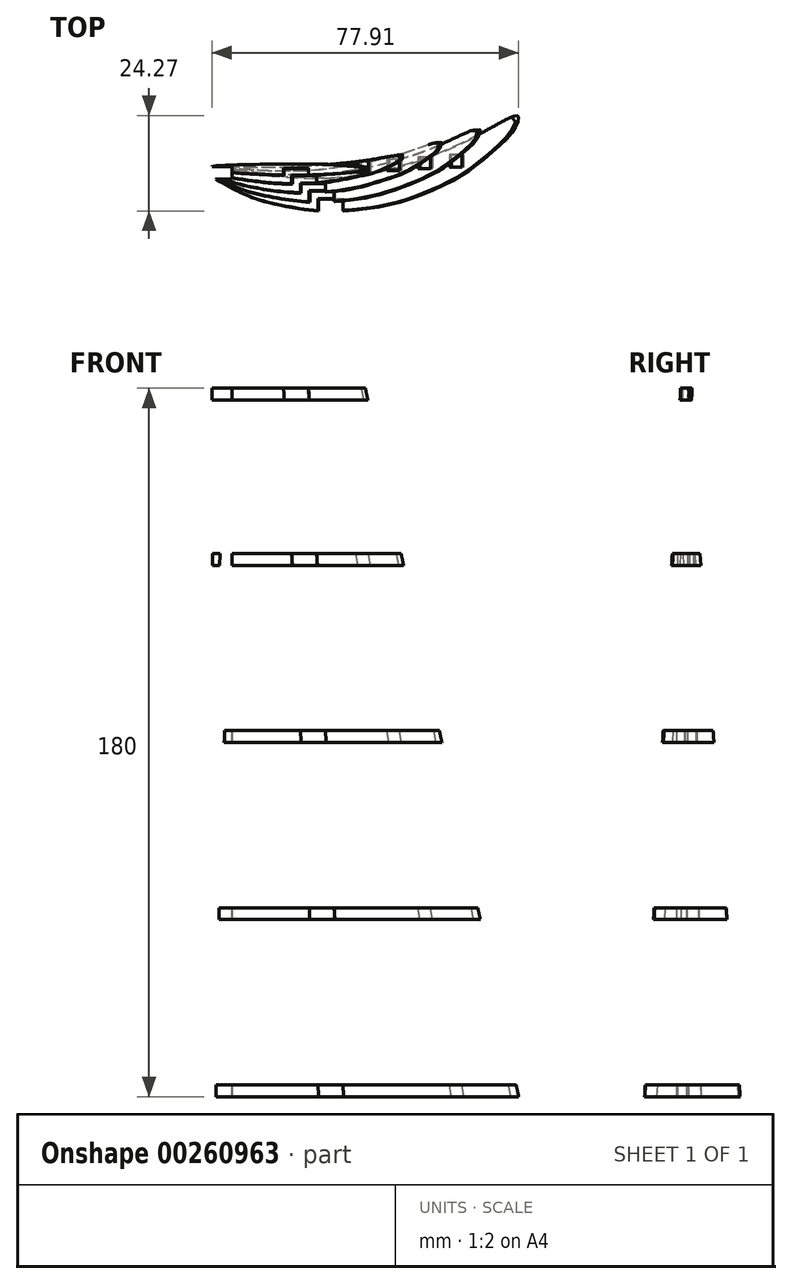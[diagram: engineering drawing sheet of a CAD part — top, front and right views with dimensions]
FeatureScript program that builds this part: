
annotation { "Feature Type Name" : "Feature", "Feature Type Description" : "" }
export const myFeature = defineFeature(function(context is Context, id is Id, definition is map)
    precondition{}
    {
        {
            var Q0;
            Q0=qCreatedBy(makeId("Top.planeOp"),FACE);
            var sketch = newSketch(context, id + "F0", { "sketchPlane" : qUnion([Q0])});
            skLineSegment(sketch, "E0", {"start": v(1.36, -2.16) * mm, "end": v(0.8, -1.48) * mm});
            skLineSegment(sketch, "E1", {"start": v(0.8, -1.48) * mm, "end": v(0.54, -1.16) * mm});
            skLineSegment(sketch, "E2", {"start": v(0.54, -1.16) * mm, "end": v(0.32, -0.85) * mm});
            skLineSegment(sketch, "E3", {"start": v(0.32, -0.85) * mm, "end": v(0.15, -0.57) * mm});
            skLineSegment(sketch, "E4", {"start": v(0.15, -0.57) * mm, "end": v(0.04, -0.32) * mm});
            skLineSegment(sketch, "E5", {"start": v(0.04, -0.32) * mm, "end": v(0, -0.1) * mm});
            skLineSegment(sketch, "E6", {"start": v(0, -0.1) * mm, "end": v(0, 0) * mm});
            skLineSegment(sketch, "E7", {"start": v(0, 0) * mm, "end": v(0.14, 0.2) * mm});
            skLineSegment(sketch, "E8", {"start": v(0.14, 0.2) * mm, "end": v(0.34, 0.3) * mm});
            skLineSegment(sketch, "E9", {"start": v(0.34, 0.3) * mm, "end": v(0.6, 0.35) * mm});
            skLineSegment(sketch, "E10", {"start": v(0.6, 0.35) * mm, "end": v(0.9, 0.37) * mm});
            skLineSegment(sketch, "E11", {"start": v(0.9, 0.37) * mm, "end": v(1.27, 0.37) * mm});
            skLineSegment(sketch, "E12", {"start": v(1.27, 0.37) * mm, "end": v(1.67, 0.35) * mm});
            skLineSegment(sketch, "E13", {"start": v(1.67, 0.35) * mm, "end": v(2.54, 0.25) * mm});
            skLineSegment(sketch, "E14", {"start": v(2.54, 0.25) * mm, "end": v(3.67, 0.08) * mm});
            skLineSegment(sketch, "E15", {"start": v(3.67, 0.08) * mm, "end": v(5.17, -0.16) * mm});
            skLineSegment(sketch, "E16", {"start": v(5.17, -0.16) * mm, "end": v(5.97, -0.3) * mm});
            skLineSegment(sketch, "E17", {"start": v(5.97, -0.3) * mm, "end": v(6.72, -0.43) * mm});
            skLineSegment(sketch, "E18", {"start": v(6.72, -0.43) * mm, "end": v(7.44, -0.55) * mm});
            skLineSegment(sketch, "E19", {"start": v(7.44, -0.55) * mm, "end": v(8.78, -0.8) * mm});
            skLineSegment(sketch, "E20", {"start": v(8.78, -0.8) * mm, "end": v(10.03, -1.02) * mm});
            skLineSegment(sketch, "E21", {"start": v(10.03, -1.02) * mm, "end": v(11.21, -1.23) * mm});
            skLineSegment(sketch, "E22", {"start": v(11.21, -1.23) * mm, "end": v(13.97, -1.68) * mm});
            skLineSegment(sketch, "E23", {"start": v(13.97, -1.68) * mm, "end": v(14.7, -1.78) * mm});
            skLineSegment(sketch, "E24", {"start": v(14.7, -1.78) * mm, "end": v(15.94, -1.94) * mm});
            skLineSegment(sketch, "E25", {"start": v(15.94, -1.94) * mm, "end": v(17.2, -2.08) * mm});
            skLineSegment(sketch, "E26", {"start": v(17.2, -2.08) * mm, "end": v(18.5, -2.2) * mm});
            skLineSegment(sketch, "E27", {"start": v(18.5, -2.2) * mm, "end": v(21.19, -2.42) * mm});
            skLineSegment(sketch, "E28", {"start": v(21.19, -2.42) * mm, "end": v(23.95, -2.56) * mm});
            skLineSegment(sketch, "E29", {"start": v(23.95, -2.56) * mm, "end": v(26.74, -2.62) * mm});
            skLineSegment(sketch, "E30", {"start": v(26.74, -2.62) * mm, "end": v(30.9, -2.55) * mm});
            skLineSegment(sketch, "E31", {"start": v(30.9, -2.55) * mm, "end": v(32.3, -2.49) * mm});
            skLineSegment(sketch, "E32", {"start": v(32.3, -2.49) * mm, "end": v(35, -2.28) * mm});
            skLineSegment(sketch, "E33", {"start": v(35, -2.28) * mm, "end": v(37.68, -1.98) * mm});
            skLineSegment(sketch, "E34", {"start": v(37.68, -1.98) * mm, "end": v(40.32, -1.59) * mm});
            skLineSegment(sketch, "E35", {"start": v(40.32, -1.59) * mm, "end": v(42.94, -1.1) * mm});
            skLineSegment(sketch, "E36", {"start": v(42.94, -1.1) * mm, "end": v(45.56, -0.51) * mm});
            skLineSegment(sketch, "E37", {"start": v(45.56, -0.51) * mm, "end": v(48.18, 0.16) * mm});
            skLineSegment(sketch, "E38", {"start": v(48.18, 0.16) * mm, "end": v(50.38, 0.8) * mm});
            skLineSegment(sketch, "E39", {"start": v(50.38, 0.8) * mm, "end": v(53.48, 1.8) * mm});
            skLineSegment(sketch, "E40", {"start": v(53.48, 1.8) * mm, "end": v(56.12, 2.73) * mm});
            skLineSegment(sketch, "E41", {"start": v(56.12, 2.73) * mm, "end": v(58.71, 3.72) * mm});
            skLineSegment(sketch, "E42", {"start": v(58.71, 3.72) * mm, "end": v(61.23, 4.76) * mm});
            skLineSegment(sketch, "E43", {"start": v(61.23, 4.76) * mm, "end": v(63.63, 5.81) * mm});
            skLineSegment(sketch, "E44", {"start": v(63.63, 5.81) * mm, "end": v(64.77, 6.34) * mm});
            skLineSegment(sketch, "E45", {"start": v(64.77, 6.34) * mm, "end": v(66.19, 7.03) * mm});
            skLineSegment(sketch, "E46", {"start": v(66.19, 7.03) * mm, "end": v(67.97, 7.93) * mm});
            skLineSegment(sketch, "E47", {"start": v(67.97, 7.93) * mm, "end": v(69, 8.48) * mm});
            skLineSegment(sketch, "E48", {"start": v(69, 8.48) * mm, "end": v(70.08, 9.07) * mm});
            skLineSegment(sketch, "E49", {"start": v(70.08, 9.07) * mm, "end": v(71.21, 9.7) * mm});
            skLineSegment(sketch, "E50", {"start": v(71.21, 9.7) * mm, "end": v(72.44, 10.38) * mm});
            skLineSegment(sketch, "E51", {"start": v(72.44, 10.38) * mm, "end": v(73.1, 10.75) * mm});
            skLineSegment(sketch, "E52", {"start": v(73.1, 10.75) * mm, "end": v(73.8, 11.14) * mm});
            skLineSegment(sketch, "E53", {"start": v(73.8, 11.14) * mm, "end": v(74.53, 11.55) * mm});
            skLineSegment(sketch, "E54", {"start": v(74.53, 11.55) * mm, "end": v(75.29, 11.98) * mm});
            skLineSegment(sketch, "E55", {"start": v(75.29, 11.98) * mm, "end": v(76.12, 12.43) * mm});
            skLineSegment(sketch, "E56", {"start": v(76.12, 12.43) * mm, "end": v(76.92, 12.85) * mm});
            skLineSegment(sketch, "E57", {"start": v(76.92, 12.85) * mm, "end": v(77.3, 13.02) * mm});
            skLineSegment(sketch, "E58", {"start": v(77.3, 13.02) * mm, "end": v(77.66, 13.17) * mm});
            skLineSegment(sketch, "E59", {"start": v(77.66, 13.17) * mm, "end": v(77.98, 13.28) * mm});
            skLineSegment(sketch, "E60", {"start": v(77.98, 13.28) * mm, "end": v(78.27, 13.34) * mm});
            skLineSegment(sketch, "E61", {"start": v(78.27, 13.34) * mm, "end": v(78.52, 13.36) * mm});
            skLineSegment(sketch, "E62", {"start": v(78.52, 13.36) * mm, "end": v(78.72, 13.31) * mm});
            skLineSegment(sketch, "E63", {"start": v(78.72, 13.31) * mm, "end": v(78.88, 13.17) * mm});
            skLineSegment(sketch, "E64", {"start": v(78.88, 13.17) * mm, "end": v(78.94, 13.03) * mm});
            skLineSegment(sketch, "E65", {"start": v(78.94, 13.03) * mm, "end": v(78.95, 12.78) * mm});
            skLineSegment(sketch, "E66", {"start": v(78.95, 12.78) * mm, "end": v(78.92, 12.48) * mm});
            skLineSegment(sketch, "E67", {"start": v(78.92, 12.48) * mm, "end": v(78.84, 12.15) * mm});
            skLineSegment(sketch, "E68", {"start": v(78.84, 12.15) * mm, "end": v(78.73, 11.78) * mm});
            skLineSegment(sketch, "E69", {"start": v(78.73, 11.78) * mm, "end": v(78.43, 11.01) * mm});
            skLineSegment(sketch, "E70", {"start": v(78.43, 11.01) * mm, "end": v(78.24, 10.62) * mm});
            skLineSegment(sketch, "E71", {"start": v(78.24, 10.62) * mm, "end": v(77.68, 9.6) * mm});
            skLineSegment(sketch, "E72", {"start": v(77.68, 9.6) * mm, "end": v(77.28, 9) * mm});
            skLineSegment(sketch, "E73", {"start": v(77.28, 9) * mm, "end": v(76.86, 8.45) * mm});
            skLineSegment(sketch, "E74", {"start": v(76.86, 8.45) * mm, "end": v(76.43, 7.94) * mm});
            skLineSegment(sketch, "E75", {"start": v(76.43, 7.94) * mm, "end": v(75.53, 7.04) * mm});
            skLineSegment(sketch, "E76", {"start": v(75.53, 7.04) * mm, "end": v(74.25, 5.9) * mm});
            skLineSegment(sketch, "E77", {"start": v(74.25, 5.9) * mm, "end": v(71.62, 3.6) * mm});
            skLineSegment(sketch, "E78", {"start": v(71.62, 3.6) * mm, "end": v(69.55, 1.83) * mm});
            skLineSegment(sketch, "E79", {"start": v(69.55, 1.83) * mm, "end": v(68.49, 0.97) * mm});
            skLineSegment(sketch, "E80", {"start": v(68.49, 0.97) * mm, "end": v(67.54, 0.24) * mm});
            skLineSegment(sketch, "E81", {"start": v(67.54, 0.24) * mm, "end": v(66.3, -0.66) * mm});
            skLineSegment(sketch, "E82", {"start": v(66.3, -0.66) * mm, "end": v(65.17, -1.41) * mm});
            skLineSegment(sketch, "E83", {"start": v(65.17, -1.41) * mm, "end": v(64.03, -2.13) * mm});
            skLineSegment(sketch, "E84", {"start": v(64.03, -2.13) * mm, "end": v(62.87, -2.8) * mm});
            skLineSegment(sketch, "E85", {"start": v(62.87, -2.8) * mm, "end": v(60.5, -4.08) * mm});
            skLineSegment(sketch, "E86", {"start": v(60.5, -4.08) * mm, "end": v(58.52, -5.03) * mm});
            skLineSegment(sketch, "E87", {"start": v(58.52, -5.03) * mm, "end": v(55.6, -6.29) * mm});
            skLineSegment(sketch, "E88", {"start": v(55.6, -6.29) * mm, "end": v(53.08, -7.24) * mm});
            skLineSegment(sketch, "E89", {"start": v(53.08, -7.24) * mm, "end": v(50.52, -8.1) * mm});
            skLineSegment(sketch, "E90", {"start": v(50.52, -8.1) * mm, "end": v(47.82, -8.86) * mm});
            skLineSegment(sketch, "E91", {"start": v(47.82, -8.86) * mm, "end": v(45.3, -9.47) * mm});
            skLineSegment(sketch, "E92", {"start": v(45.3, -9.47) * mm, "end": v(42.66, -10) * mm});
            skLineSegment(sketch, "E93", {"start": v(42.66, -10) * mm, "end": v(40, -10.4) * mm});
            skLineSegment(sketch, "E94", {"start": v(40, -10.4) * mm, "end": v(36.49, -10.78) * mm});
            skLineSegment(sketch, "E95", {"start": v(36.49, -10.78) * mm, "end": v(34.63, -10.9) * mm});
            skLineSegment(sketch, "E96", {"start": v(34.63, -10.9) * mm, "end": v(31.94, -10.96) * mm});
            skLineSegment(sketch, "E97", {"start": v(31.94, -10.96) * mm, "end": v(29.24, -10.91) * mm});
            skLineSegment(sketch, "E98", {"start": v(29.24, -10.91) * mm, "end": v(26.55, -10.75) * mm});
            skLineSegment(sketch, "E99", {"start": v(26.55, -10.75) * mm, "end": v(25.15, -10.62) * mm});
            skLineSegment(sketch, "E100", {"start": v(25.15, -10.62) * mm, "end": v(21.2, -10.07) * mm});
            skLineSegment(sketch, "E101", {"start": v(21.2, -10.07) * mm, "end": v(18.56, -9.56) * mm});
            skLineSegment(sketch, "E102", {"start": v(18.56, -9.56) * mm, "end": v(14.85, -8.62) * mm});
            skLineSegment(sketch, "E103", {"start": v(14.85, -8.62) * mm, "end": v(13.35, -8.17) * mm});
            skLineSegment(sketch, "E104", {"start": v(13.35, -8.17) * mm, "end": v(12.07, -7.74) * mm});
            skLineSegment(sketch, "E105", {"start": v(12.07, -7.74) * mm, "end": v(10.8, -7.28) * mm});
            skLineSegment(sketch, "E106", {"start": v(10.8, -7.28) * mm, "end": v(9.55, -6.77) * mm});
            skLineSegment(sketch, "E107", {"start": v(9.55, -6.77) * mm, "end": v(8.32, -6.23) * mm});
            skLineSegment(sketch, "E108", {"start": v(8.32, -6.23) * mm, "end": v(6.7, -5.43) * mm});
            skLineSegment(sketch, "E109", {"start": v(6.7, -5.43) * mm, "end": v(5.93, -5) * mm});
            skLineSegment(sketch, "E110", {"start": v(5.93, -5) * mm, "end": v(4.77, -4.33) * mm});
            skLineSegment(sketch, "E111", {"start": v(4.77, -4.33) * mm, "end": v(3.62, -3.62) * mm});
            skLineSegment(sketch, "E112", {"start": v(3.62, -3.62) * mm, "end": v(1.36, -2.16) * mm});
            skSolve(sketch);
        }
        {
            var Q0;
            Q0=qCreatedBy(makeId("Top.planeOp"),FACE);
            cPlane(context, id + "F1", {"entities" : qUnion([Q0]), "cplaneType" : CPlaneType.OFFSET, "offset" : 180 * mm, "width" : 150 * mm, "height" : 150 * mm});
        }
        {
            var Q0;
            Q0=qCreatedBy(id+"F1.planeOp",FACE);
            var sketch = newSketch(context, id + "F2", { "sketchPlane" : qUnion([Q0])});
            skLineSegment(sketch, "E113", {"start": v(0, 0) * mm, "end": v(1.12, 0.44) * mm});
            skLineSegment(sketch, "E114", {"start": v(1.12, 0.44) * mm, "end": v(3.58, 0.68) * mm});
            skLineSegment(sketch, "E115", {"start": v(3.58, 0.68) * mm, "end": v(4.55, 0.76) * mm});
            skLineSegment(sketch, "E116", {"start": v(4.55, 0.76) * mm, "end": v(6.06, 0.84) * mm});
            skLineSegment(sketch, "E117", {"start": v(6.06, 0.84) * mm, "end": v(8.53, 0.9) * mm});
            skLineSegment(sketch, "E118", {"start": v(8.53, 0.9) * mm, "end": v(9.9, 0.92) * mm});
            skLineSegment(sketch, "E119", {"start": v(9.9, 0.92) * mm, "end": v(16.49, 1) * mm});
            skLineSegment(sketch, "E120", {"start": v(16.49, 1) * mm, "end": v(18.45, 1) * mm});
            skLineSegment(sketch, "E121", {"start": v(18.45, 1) * mm, "end": v(20.93, 0.98) * mm});
            skLineSegment(sketch, "E122", {"start": v(20.93, 0.98) * mm, "end": v(23.51, 0.96) * mm});
            skLineSegment(sketch, "E123", {"start": v(23.51, 0.96) * mm, "end": v(28.33, 0.9) * mm});
            skLineSegment(sketch, "E124", {"start": v(28.33, 0.9) * mm, "end": v(30.1, 0.84) * mm});
            skLineSegment(sketch, "E125", {"start": v(30.1, 0.84) * mm, "end": v(30.86, 0.8) * mm});
            skLineSegment(sketch, "E126", {"start": v(30.86, 0.8) * mm, "end": v(32.13, 0.72) * mm});
            skLineSegment(sketch, "E127", {"start": v(32.13, 0.72) * mm, "end": v(33.4, 0.64) * mm});
            skLineSegment(sketch, "E128", {"start": v(33.4, 0.64) * mm, "end": v(34, 0.61) * mm});
            skLineSegment(sketch, "E129", {"start": v(34, 0.61) * mm, "end": v(34.6, 0.58) * mm});
            skLineSegment(sketch, "E130", {"start": v(34.6, 0.58) * mm, "end": v(35.45, 0.56) * mm});
            skLineSegment(sketch, "E131", {"start": v(35.45, 0.56) * mm, "end": v(35.75, 0.56) * mm});
            skLineSegment(sketch, "E132", {"start": v(35.75, 0.56) * mm, "end": v(36.3, 0.55) * mm});
            skLineSegment(sketch, "E133", {"start": v(36.3, 0.55) * mm, "end": v(36.86, 0.53) * mm});
            skLineSegment(sketch, "E134", {"start": v(36.86, 0.53) * mm, "end": v(37.46, 0.48) * mm});
            skLineSegment(sketch, "E135", {"start": v(37.46, 0.48) * mm, "end": v(37.78, 0.44) * mm});
            skLineSegment(sketch, "E136", {"start": v(37.78, 0.44) * mm, "end": v(38.12, 0.4) * mm});
            skLineSegment(sketch, "E137", {"start": v(38.12, 0.4) * mm, "end": v(38.48, 0.33) * mm});
            skLineSegment(sketch, "E138", {"start": v(38.48, 0.33) * mm, "end": v(38.88, 0.24) * mm});
            skLineSegment(sketch, "E139", {"start": v(38.88, 0.24) * mm, "end": v(39.26, 0.15) * mm});
            skLineSegment(sketch, "E140", {"start": v(39.26, 0.15) * mm, "end": v(39.45, 0.1) * mm});
            skLineSegment(sketch, "E141", {"start": v(39.45, 0.1) * mm, "end": v(39.62, 0.03) * mm});
            skLineSegment(sketch, "E142", {"start": v(39.62, 0.03) * mm, "end": v(39.77, -0.03) * mm});
            skLineSegment(sketch, "E143", {"start": v(39.77, -0.03) * mm, "end": v(39.9, -0.09) * mm});
            skLineSegment(sketch, "E144", {"start": v(39.9, -0.09) * mm, "end": v(39.97, -0.15) * mm});
            skLineSegment(sketch, "E145", {"start": v(39.97, -0.15) * mm, "end": v(40, -0.2) * mm});
            skLineSegment(sketch, "E146", {"start": v(40, -0.2) * mm, "end": v(39.98, -0.27) * mm});
            skLineSegment(sketch, "E147", {"start": v(39.98, -0.27) * mm, "end": v(39.9, -0.32) * mm});
            skLineSegment(sketch, "E148", {"start": v(39.9, -0.32) * mm, "end": v(39.8, -0.38) * mm});
            skLineSegment(sketch, "E149", {"start": v(39.8, -0.38) * mm, "end": v(39.65, -0.44) * mm});
            skLineSegment(sketch, "E150", {"start": v(39.65, -0.44) * mm, "end": v(39.48, -0.49) * mm});
            skLineSegment(sketch, "E151", {"start": v(39.48, -0.49) * mm, "end": v(39.29, -0.54) * mm});
            skLineSegment(sketch, "E152", {"start": v(39.29, -0.54) * mm, "end": v(38.68, -0.68) * mm});
            skLineSegment(sketch, "E153", {"start": v(38.68, -0.68) * mm, "end": v(38.47, -0.72) * mm});
            skLineSegment(sketch, "E154", {"start": v(38.47, -0.72) * mm, "end": v(38.08, -0.8) * mm});
            skLineSegment(sketch, "E155", {"start": v(38.08, -0.8) * mm, "end": v(37.73, -0.87) * mm});
            skLineSegment(sketch, "E156", {"start": v(37.73, -0.87) * mm, "end": v(37.4, -0.92) * mm});
            skLineSegment(sketch, "E157", {"start": v(37.4, -0.92) * mm, "end": v(37.08, -0.98) * mm});
            skLineSegment(sketch, "E158", {"start": v(37.08, -0.98) * mm, "end": v(36.79, -1.02) * mm});
            skLineSegment(sketch, "E159", {"start": v(36.79, -1.02) * mm, "end": v(36.22, -1.1) * mm});
            skLineSegment(sketch, "E160", {"start": v(36.22, -1.1) * mm, "end": v(35.69, -1.15) * mm});
            skLineSegment(sketch, "E161", {"start": v(35.69, -1.15) * mm, "end": v(35.17, -1.2) * mm});
            skLineSegment(sketch, "E162", {"start": v(35.17, -1.2) * mm, "end": v(34.59, -1.25) * mm});
            skLineSegment(sketch, "E163", {"start": v(34.59, -1.25) * mm, "end": v(34, -1.3) * mm});
            skLineSegment(sketch, "E164", {"start": v(34, -1.3) * mm, "end": v(33.4, -1.34) * mm});
            skLineSegment(sketch, "E165", {"start": v(33.4, -1.34) * mm, "end": v(32.14, -1.42) * mm});
            skLineSegment(sketch, "E166", {"start": v(32.14, -1.42) * mm, "end": v(29.86, -1.56) * mm});
            skLineSegment(sketch, "E167", {"start": v(29.86, -1.56) * mm, "end": v(28.31, -1.63) * mm});
            skLineSegment(sketch, "E168", {"start": v(28.31, -1.63) * mm, "end": v(27.07, -1.67) * mm});
            skLineSegment(sketch, "E169", {"start": v(27.07, -1.67) * mm, "end": v(23.4, -1.76) * mm});
            skLineSegment(sketch, "E170", {"start": v(23.4, -1.76) * mm, "end": v(22.16, -1.77) * mm});
            skLineSegment(sketch, "E171", {"start": v(22.16, -1.77) * mm, "end": v(19.69, -1.76) * mm});
            skLineSegment(sketch, "E172", {"start": v(19.69, -1.76) * mm, "end": v(16.57, -1.72) * mm});
            skLineSegment(sketch, "E173", {"start": v(16.57, -1.72) * mm, "end": v(14.72, -1.67) * mm});
            skLineSegment(sketch, "E174", {"start": v(14.72, -1.67) * mm, "end": v(12.24, -1.56) * mm});
            skLineSegment(sketch, "E175", {"start": v(12.24, -1.56) * mm, "end": v(10.14, -1.44) * mm});
            skLineSegment(sketch, "E176", {"start": v(10.14, -1.44) * mm, "end": v(4.83, -1) * mm});
            skLineSegment(sketch, "E177", {"start": v(4.83, -1) * mm, "end": v(3.6, -0.9) * mm});
            skLineSegment(sketch, "E178", {"start": v(3.6, -0.9) * mm, "end": v(2.97, -0.82) * mm});
            skLineSegment(sketch, "E179", {"start": v(2.97, -0.82) * mm, "end": v(2.36, -0.72) * mm});
            skLineSegment(sketch, "E180", {"start": v(2.36, -0.72) * mm, "end": v(1.76, -0.6) * mm});
            skLineSegment(sketch, "E181", {"start": v(1.76, -0.6) * mm, "end": v(1.32, -0.48) * mm});
            skLineSegment(sketch, "E182", {"start": v(1.32, -0.48) * mm, "end": v(0.58, -0.23) * mm});
            skLineSegment(sketch, "E183", {"start": v(0.58, -0.23) * mm, "end": v(0, 0) * mm});
            skSolve(sketch);
        }
        {
            var Q0;
            Q0=qCreatedBy(makeId("Top.planeOp"),FACE);
            var sketch = newSketch(context, id + "F3", { "sketchPlane" : qUnion([Q0])});
            skPoint(sketch, "E184.0", {"position": v(0.34, 0.3) * mm});
            skPoint(sketch, "E184.1", {"position": v(0.14, 0.2) * mm});
            skPoint(sketch, "E184.2", {"position": v(0, 0) * mm});
            skPoint(sketch, "E184.3", {"position": v(0, -0.1) * mm});
            skPoint(sketch, "E184.4", {"position": v(0.04, -0.32) * mm});
            skPoint(sketch, "E184.5", {"position": v(1.36, -2.16) * mm});
            skPoint(sketch, "E184.6", {"position": v(4.77, -4.33) * mm});
            skPoint(sketch, "E184.7", {"position": v(14.85, -8.62) * mm});
            skPoint(sketch, "E184.8", {"position": v(9.55, -6.77) * mm});
            skPoint(sketch, "E184.9", {"position": v(25.15, -10.62) * mm});
            skPoint(sketch, "E184.10", {"position": v(31.94, -10.96) * mm});
            skPoint(sketch, "E184.11", {"position": v(42.66, -10) * mm});
            skPoint(sketch, "E184.12", {"position": v(53.08, -7.24) * mm});
            skPoint(sketch, "E184.13", {"position": v(62.87, -2.8) * mm});
            skPoint(sketch, "E184.14", {"position": v(68.49, 0.97) * mm});
            skPoint(sketch, "E184.15", {"position": v(75.53, 7.04) * mm});
            skPoint(sketch, "E184.16", {"position": v(78.24, 10.62) * mm});
            skPoint(sketch, "E184.17", {"position": v(78.95, 12.78) * mm});
            skPoint(sketch, "E184.18", {"position": v(78.88, 13.17) * mm});
            skPoint(sketch, "E184.19", {"position": v(78.52, 13.36) * mm});
            skPoint(sketch, "E184.20", {"position": v(76.92, 12.85) * mm});
            skPoint(sketch, "E184.21", {"position": v(74.53, 11.55) * mm});
            skPoint(sketch, "E184.22", {"position": v(70.08, 9.07) * mm});
            skPoint(sketch, "E184.23", {"position": v(63.63, 5.81) * mm});
            skPoint(sketch, "E184.24", {"position": v(56.12, 2.73) * mm});
            skPoint(sketch, "E184.25", {"position": v(50.38, 0.8) * mm});
            skPoint(sketch, "E184.26", {"position": v(45.56, -0.51) * mm});
            skPoint(sketch, "E184.27", {"position": v(35, -2.28) * mm});
            skPoint(sketch, "E184.28", {"position": v(30.9, -2.55) * mm});
            skPoint(sketch, "E184.29", {"position": v(23.95, -2.56) * mm});
            skPoint(sketch, "E184.30", {"position": v(17.2, -2.08) * mm});
            skPoint(sketch, "E184.31", {"position": v(13.97, -1.68) * mm});
            skPoint(sketch, "E184.32", {"position": v(11.21, -1.23) * mm});
            skPoint(sketch, "E184.33", {"position": v(5.97, -0.3) * mm});
            skPoint(sketch, "E184.34", {"position": v(1.67, 0.35) * mm});
            skPoint(sketch, "E184.35", {"position": v(0.9, 0.37) * mm});
            skFitSpline(sketch, "E185", {"points": [v(0, 0) * mm, v(0, -0.1) * mm, v(0.04, -0.32) * mm, v(1.36, -2.16) * mm, v(4.77, -4.33) * mm, v(9.55, -6.77) * mm, v(14.85, -8.62) * mm, v(25.15, -10.62) * mm, v(31.94, -10.96) * mm, v(42.66, -10) * mm, v(53.08, -7.24) * mm, v(62.87, -2.8) * mm, v(68.49, 0.97) * mm, v(75.53, 7.04) * mm, v(78.24, 10.62) * mm, v(78.95, 12.78) * mm, v(78.88, 13.17) * mm, v(78.52, 13.36) * mm, v(76.92, 12.85) * mm], "startDerivative": vector(-1.46, -11.53) * mm, "endDerivative": vector(-52.48, -22.5) * mm});
            skFitSpline(sketch, "E186", {"points": [v(0, 0) * mm, v(0.14, 0.2) * mm, v(0.34, 0.3) * mm, v(0.9, 0.37) * mm, v(1.67, 0.35) * mm, v(5.97, -0.3) * mm, v(11.21, -1.23) * mm, v(13.97, -1.68) * mm, v(17.2, -2.08) * mm, v(23.95, -2.56) * mm, v(30.9, -2.55) * mm, v(35, -2.28) * mm, v(45.56, -0.51) * mm, v(50.38, 0.8) * mm, v(56.12, 2.73) * mm, v(63.63, 5.81) * mm, v(70.08, 9.07) * mm, v(74.53, 11.55) * mm, v(76.92, 12.85) * mm], "startDerivative": vector(9.67, 15.95) * mm, "endDerivative": vector(47.44, 25.3) * mm});
            skSolve(sketch);
        }
        {
            var Q0;
            Q0=qCreatedBy(id+"F1.planeOp",FACE);
            var sketch = newSketch(context, id + "F4", { "sketchPlane" : qUnion([Q0])});
            skPoint(sketch, "E187.0", {"position": v(0, 0) * mm});
            skPoint(sketch, "E187.1", {"position": v(0.58, -0.23) * mm});
            skPoint(sketch, "E187.2", {"position": v(1.12, 0.44) * mm});
            skPoint(sketch, "E187.3", {"position": v(3.58, 0.68) * mm});
            skPoint(sketch, "E187.4", {"position": v(9.9, 0.92) * mm});
            skPoint(sketch, "E187.5", {"position": v(18.45, 1) * mm});
            skPoint(sketch, "E187.6", {"position": v(28.33, 0.9) * mm});
            skPoint(sketch, "E187.7", {"position": v(35.45, 0.56) * mm});
            skPoint(sketch, "E187.8", {"position": v(38.88, 0.24) * mm});
            skPoint(sketch, "E187.9", {"position": v(39.77, -0.03) * mm});
            skPoint(sketch, "E187.10", {"position": v(39.98, -0.27) * mm});
            skPoint(sketch, "E187.11", {"position": v(39.8, -0.38) * mm});
            skPoint(sketch, "E187.12", {"position": v(39.65, -0.44) * mm});
            skPoint(sketch, "E187.13", {"position": v(39.9, -0.09) * mm});
            skPoint(sketch, "E187.14", {"position": v(37.4, -0.92) * mm});
            skPoint(sketch, "E187.15", {"position": v(35.17, -1.2) * mm});
            skPoint(sketch, "E187.16", {"position": v(28.31, -1.63) * mm});
            skPoint(sketch, "E187.17", {"position": v(23.4, -1.76) * mm});
            skPoint(sketch, "E187.18", {"position": v(16.57, -1.72) * mm});
            skPoint(sketch, "E187.19", {"position": v(10.14, -1.44) * mm});
            skPoint(sketch, "E187.20", {"position": v(3.6, -0.9) * mm});
            skPoint(sketch, "E187.21", {"position": v(1.54, -0.54) * mm});
            skPoint(sketch, "E188.0", {"position": v(40, -0.2) * mm});
            skFitSpline(sketch, "E189", {"points": [v(0, 0) * mm, v(1.12, 0.44) * mm, v(3.58, 0.68) * mm, v(9.9, 0.92) * mm, v(18.45, 1) * mm, v(28.1, 1) * mm, v(35.45, 0.56) * mm, v(38.88, 0.24) * mm], "startDerivative": vector(14.83, 7.14) * mm, "endDerivative": vector(26.49, -3.98) * mm});
            skFitSpline(sketch, "E190", {"points": [v(0, 0) * mm, v(0.58, -0.23) * mm, v(1.54, -0.54) * mm, v(3.6, -0.9) * mm, v(10.14, -1.44) * mm, v(16.57, -1.72) * mm, v(23.4, -1.76) * mm, v(28.31, -1.63) * mm, v(35.17, -1.2) * mm, v(37.4, -0.92) * mm, v(39.65, -0.44) * mm, v(39.8, -0.38) * mm, v(39.98, -0.27) * mm, v(40, -0.18) * mm, v(39.9, -0.09) * mm, v(39.77, -0.03) * mm, v(38.88, 0.24) * mm], "startDerivative": vector(15.05, -6) * mm, "endDerivative": vector(-40.6, 7.91) * mm});
            skSolve(sketch);
        }
        {
            var Q0;
            Q0=makeQuery(id+"F4.imprint","IMPRINT",FACE,{"disambiguationData":[TD([[makeQuery(id+"F4.imprint","IMPRINT",EDGE,{"derivedFrom":sQuery(id+"F4.wireOp",EDGE,"E189")}),-1.0]])]});
            var Q1;
            Q1=makeQuery(id+"F3.imprint","IMPRINT",FACE,{"disambiguationData":[TD([[makeQuery(id+"F3.imprint","IMPRINT",EDGE,{"derivedFrom":sQuery(id+"F3.wireOp",EDGE,"E185")}),1.0]])]});
            loft(context, id + "F5", {"sheetProfilesArray" : [{ "sheetProfileEntities" : qUnion([Q0]) }, { "sheetProfileEntities" : qUnion([Q1]) }]});
        }
        {
            var Q0;
            Q0=qCreatedBy(id+"F1.planeOp",FACE);
            var sketch = newSketch(context, id + "F6", { "sketchPlane" : qUnion([Q0])});
            skLineSegment(sketch, "E191.bottom", {"start": v(6.17, -2.75) * mm, "end": v(-0.18, -2.75) * mm});
            skLineSegment(sketch, "E191.top", {"start": v(6.17, 0.42) * mm, "end": v(-0.18, 0.42) * mm});
            skLineSegment(sketch, "E191.left", {"start": v(6.17, -2.75) * mm, "end": v(6.17, 0.42) * mm});
            skLineSegment(sketch, "E191.right", {"start": v(-0.18, -2.75) * mm, "end": v(-0.18, 0.42) * mm});
            skLineSegment(sketch, "E192.bottom", {"start": v(25.59, -3.13) * mm, "end": v(19.24, -3.13) * mm});
            skLineSegment(sketch, "E192.top", {"start": v(25.59, 0.05) * mm, "end": v(19.24, 0.05) * mm});
            skLineSegment(sketch, "E192.left", {"start": v(25.59, -3.13) * mm, "end": v(25.59, 0.05) * mm});
            skLineSegment(sketch, "E192.right", {"start": v(19.24, -3.13) * mm, "end": v(19.24, 0.05) * mm});
            skSolve(sketch);
        }
        {
            var Q0;
            Q0=makeQuery(id+"F5.opLoft","CAP_FACE",FACE,{"disambiguationData":[OSD([makeQuery(id+"F3.imprint","IMPRINT",FACE,{"disambiguationData":[TD([[makeQuery(id+"F3.imprint","IMPRINT",EDGE,{"derivedFrom":sQuery(id+"F3.wireOp",EDGE,"E185")}),1.0]])]})])],"isStart":true});
            var sketch = newSketch(context, id + "F7", { "sketchPlane" : qUnion([Q0])});
            skLineSegment(sketch, "E193.0", {"start": v(-0.18, 2.75) * mm, "end": v(-0.18, -0.42) * mm});
            skLineSegment(sketch, "E193.1", {"start": v(6.17, 2.75) * mm, "end": v(-0.18, 2.75) * mm});
            skLineSegment(sketch, "E193.2", {"start": v(6.17, 2.75) * mm, "end": v(6.17, -0.42) * mm});
            skLineSegment(sketch, "E193.3", {"start": v(6.17, -0.42) * mm, "end": v(-0.18, -0.42) * mm});
            skPoint(sketch, "E194.0", {"position": v(-0.18, -0.42) * mm});
            skLineSegment(sketch, "E195.0", {"start": v(28.12, 11.03) * mm, "end": v(28.12, 7.86) * mm});
            skLineSegment(sketch, "E195.1", {"start": v(34.47, 11.03) * mm, "end": v(28.12, 11.03) * mm});
            skLineSegment(sketch, "E195.2", {"start": v(34.47, 11.03) * mm, "end": v(34.47, 7.86) * mm});
            skLineSegment(sketch, "E195.3", {"start": v(34.47, 7.86) * mm, "end": v(28.12, 7.86) * mm});
            skPoint(sketch, "E196.0", {"position": v(28.12, 7.86) * mm});
            skLineSegment(sketch, "E197.0", {"start": v(61.84, -0.31) * mm, "end": v(61.84, -3.49) * mm});
            skLineSegment(sketch, "E197.1", {"start": v(65.02, -0.31) * mm, "end": v(61.84, -0.31) * mm});
            skLineSegment(sketch, "E197.2", {"start": v(65.02, -0.31) * mm, "end": v(65.02, -3.49) * mm});
            skLineSegment(sketch, "E197.3", {"start": v(65.02, -3.49) * mm, "end": v(61.84, -3.49) * mm});
            skPoint(sketch, "E198.0", {"position": v(61.84, -3.49) * mm});
            skSolve(sketch);
        }
        {
            var Q1;
            Q1=makeQuery(id+"F6.imprint","IMPRINT",FACE,{"disambiguationData":[TD([[makeQuery(id+"F6.imprint","IMPRINT",EDGE,{"derivedFrom":sQuery(id+"F6.wireOp",EDGE,"E192.bottom")}),-1.0]])]});
            var Q2;
            {var subQ0=sQuery(id+"F7.wireOp",EDGE,"E195.3");Q2=makeQuery(id+"F7.imprint","IMPRINT",FACE,{"disambiguationData":[TD([[makeQuery(id+"F7.imprint","IMPRINT",EDGE,{"derivedFrom":subQ0}),-1.0]])]});}
            loft(context, id + "F8", {"operationType" : NewBodyOperationType.REMOVE, "sheetProfilesArray" : [{ "sheetProfileEntities" : qUnion([Q1]) }, { "sheetProfileEntities" : qUnion([Q2]) }]});
        }
        {
            var Q0;
            Q0=sQuery(id+"F6.wireOp",VERTEX,"E191.right.end");
            var Q1;
            Q1=sQuery(id+"F6.wireOp",VERTEX,"E191.right.start");
            var Q2;
            Q2=sQuery(id+"F7.wireOp",VERTEX,"E193.0.start");
            cPlane(context, id + "F9", {"entities" : qUnion([Q0, Q1, Q2]), "cplaneType" : CPlaneType.THREE_POINT, "offset" : 25 * mm, "width" : 150 * mm, "height" : 150 * mm});
        }
        {
            var Q0;
            Q0=qCreatedBy(id+"F9.planeOp",FACE);
            var sketch = newSketch(context, id + "F10", { "sketchPlane" : qUnion([Q0])});
            skLineSegment(sketch, "E199", {"start": v(-0.42, 0) * mm, "end": v(-0.42, 180) * mm});
            skSolve(sketch);
        }
        {
            var Q0;
            {var subQ0=sQuery(id+"F7.wireOp",EDGE,"E193.2");var subQ1=sQuery(id+"F7.wireOp",EDGE,"E193.1");var subQ2=makeQuery(id+"F7.imprint","INTERSECT",VERTEX,{"derivedFrom":[subQ1,subQ0]});Q0=makeQuery(id+"F7.imprint","IMPRINT",FACE,{"disambiguationData":[TD([[makeQuery(id+"F7.imprint","IMPRINT",EDGE,{"disambiguationData":[TD([[subQ2,-1.0]])],"derivedFrom":subQ1}),1.0]])]});}
            var Q1;
            {var subQ9=sQuery(id+"F7.wireOp",EDGE,"E193.0");Q1=makeQuery(id+"F7.imprint","IMPRINT",FACE,{"disambiguationData":[TD([[makeQuery(id+"F7.imprint","IMPRINT",EDGE,{"derivedFrom":subQ9}),1.0]])]});}
            var Q2;
            Q2=sQuery(id+"F10.wireOp",EDGE,"E199");
            sweep(context, id + "F11", {"operationType" : NewBodyOperationType.REMOVE, "profiles" : qUnion([Q0, Q1]), "path" : qUnion([Q2])});
        }
        {
            var Q0;
            Q0=qCreatedBy(makeId("Front.planeOp"),FACE);
            var sketch = newSketch(context, id + "F12", { "sketchPlane" : qUnion([Q0])});
            skLineSegment(sketch, "E200", {"start": v(0, 0) * mm, "end": v(0, 3) * mm, "construction": true});
            skLineSegment(sketch, "E201.bottom", {"start": v(0, 3) * mm, "end": v(90, 3) * mm});
            skLineSegment(sketch, "E201.top", {"start": v(0, 45) * mm, "end": v(90, 45) * mm});
            skLineSegment(sketch, "E201.left", {"start": v(0, 3) * mm, "end": v(0, 45) * mm});
            skLineSegment(sketch, "E201.right", {"start": v(90, 3) * mm, "end": v(90, 45) * mm});
            skLineSegment(sketch, "E202", {"start": v(0, 45) * mm, "end": v(0, 48) * mm, "construction": true});
            skLineSegment(sketch, "E203.bottom", {"start": v(0, 48) * mm, "end": v(90, 48) * mm});
            skLineSegment(sketch, "E203.top", {"start": v(0, 90) * mm, "end": v(90, 90) * mm});
            skLineSegment(sketch, "E203.left", {"start": v(0, 48) * mm, "end": v(0, 90) * mm});
            skLineSegment(sketch, "E203.right", {"start": v(90, 48) * mm, "end": v(90, 90) * mm});
            skLineSegment(sketch, "E204", {"start": v(0, 90) * mm, "end": v(0, 93) * mm, "construction": true});
            skLineSegment(sketch, "E205.bottom", {"start": v(0, 93) * mm, "end": v(90, 93) * mm});
            skLineSegment(sketch, "E205.top", {"start": v(0, 135) * mm, "end": v(90, 135) * mm});
            skLineSegment(sketch, "E205.left", {"start": v(0, 93) * mm, "end": v(0, 135) * mm});
            skLineSegment(sketch, "E205.right", {"start": v(90, 93) * mm, "end": v(90, 135) * mm});
            skLineSegment(sketch, "E206", {"start": v(0, 135) * mm, "end": v(0, 138) * mm, "construction": true});
            skLineSegment(sketch, "E207.bottom", {"start": v(0, 138) * mm, "end": v(90, 138) * mm});
            skLineSegment(sketch, "E207.top", {"start": v(0, 177) * mm, "end": v(90, 177) * mm});
            skLineSegment(sketch, "E207.left", {"start": v(0, 138) * mm, "end": v(0, 177) * mm});
            skLineSegment(sketch, "E207.right", {"start": v(90, 138) * mm, "end": v(90, 177) * mm});
            skSolve(sketch);
        }
        {
            var Q0;
            Q0=makeQuery(id+"F12.imprint","IMPRINT",FACE,{"disambiguationData":[TD([[makeQuery(id+"F12.imprint","IMPRINT",EDGE,{"derivedFrom":sQuery(id+"F12.wireOp",EDGE,"E207.bottom")}),1.0]])]});
            var Q1;
            Q1=makeQuery(id+"F12.imprint","IMPRINT",FACE,{"disambiguationData":[TD([[makeQuery(id+"F12.imprint","IMPRINT",EDGE,{"derivedFrom":sQuery(id+"F12.wireOp",EDGE,"E205.bottom")}),1.0]])]});
            var Q2;
            Q2=makeQuery(id+"F12.imprint","IMPRINT",FACE,{"disambiguationData":[TD([[makeQuery(id+"F12.imprint","IMPRINT",EDGE,{"derivedFrom":sQuery(id+"F12.wireOp",EDGE,"E203.bottom")}),1.0]])]});
            var Q3;
            Q3=makeQuery(id+"F12.imprint","IMPRINT",FACE,{"disambiguationData":[TD([[makeQuery(id+"F12.imprint","IMPRINT",EDGE,{"derivedFrom":sQuery(id+"F12.wireOp",EDGE,"E201.bottom")}),1.0]])]});
            extrude(context, id + "F13", {"entities" : qUnion([Q0, Q1, Q2, Q3]), "operationType" : NewBodyOperationType.REMOVE, "endBound" : BoundingType.SYMMETRIC, "oppositeDirection" : true, "depth" : 115 * mm, "offsetDistance" : 25 * mm});
        }
        {
            var Q0;
            Q0=makeQuery(id+"F13.boolean.opBoolean","COPY",FACE,{"disambiguationData":[TD([makeQuery(id+"F11.boolean.opBoolean","COPY",FACE,{"derivedFrom":makeQuery(id+"F11.opSweep","SWEPT_FACE",FACE,{"disambiguationData":[OSD([sQuery(id+"F7.wireOp",EDGE,"E193.2"),sQuery(id+"F10.wireOp",EDGE,"E199")])]})})])],"derivedFrom":makeQuery(id+"F13.opExtrude","SWEPT_FACE",FACE,{"disambiguationData":[OSD([sQuery(id+"F12.wireOp",EDGE,"E207.bottom")])]})});
            var sketch = newSketch(context, id + "F14", { "sketchPlane" : qUnion([Q0])});
            skLineSegment(sketch, "E208.bottom", {"start": v(37.61, -1) * mm, "end": v(40.79, -1) * mm});
            skLineSegment(sketch, "E208.top", {"start": v(37.61, 2.17) * mm, "end": v(40.79, 2.17) * mm});
            skLineSegment(sketch, "E208.left", {"start": v(37.61, -1) * mm, "end": v(37.61, 2.17) * mm});
            skLineSegment(sketch, "E208.right", {"start": v(40.79, -1) * mm, "end": v(40.79, 2.17) * mm});
            skSolve(sketch);
        }
        {
            var Q0;
            Q0=makeQuery(id+"F7.imprint","IMPRINT",FACE,{"disambiguationData":[TD([[makeQuery(id+"F7.imprint","IMPRINT",EDGE,{"derivedFrom":sQuery(id+"F7.wireOp",EDGE,"E197.0")}),1.0]])]});
            var Q1;
            {var subQ0=sQuery(id+"F14.wireOp",EDGE,"E208.bottom");Q1=makeQuery(id+"F14.imprint","IMPRINT",FACE,{"disambiguationData":[TD([[makeQuery(id+"F14.imprint","IMPRINT",EDGE,{"derivedFrom":subQ0}),1.0]])]});}
            loft(context, id + "F15", {"operationType" : NewBodyOperationType.REMOVE, "sheetProfilesArray" : [{ "sheetProfileEntities" : qUnion([Q0]) }, { "sheetProfileEntities" : qUnion([Q1]) }]});
        }
    });
